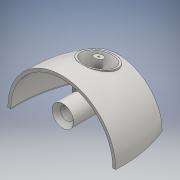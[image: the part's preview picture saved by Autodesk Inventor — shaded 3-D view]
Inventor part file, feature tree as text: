
AUTODESK INVENTOR PART (.ipt)
format: ipt  version: 2016 (Build 200138000, 138)  size: 376,320 bytes
history: native  units: mm
features: sketch x16, extrude x8, plane x6, other x4, loft x3, hole x2, shell x1, chamfer x1
ambient origin geometry x8: Origin, YZ Plane, XZ Plane, XY Plane, X Axis, Y Axis, Z Axis, Center Point
bodies: Solid1 (feature_tree)
feature tree (41):
  sketch  "Sketch1"  dims[d0=32.5mm d1=17.0mm]
  plane  "Work Plane1"
  sketch  "Sketch2"  dims[d2=26.5mm d3=4.0mm d4=32.5mm]
  plane  "Work Plane2"
  loft  "Loft1"
  extrude  "Extrusion1"  Depth=4.0mm
  plane  "Work Plane3"
  sketch  "Sketch5"  dims[d14=10.0mm d15=11.0mm]
  shell  "Shell1"  Thickness=32.5mm
  extrude  "Extrusion2"  TaperAngle=0.0deg  [1 undecoded]
  hole  "Hole1"  [1 undecoded]
  chamfer  "Chamfer1"  Distance=10.0mm
  extrude  "Extrusion3"  Depth=10.0mm
  plane  "Work Plane4"
  extrude  "Extrusion4"  Depth=0.9mm
  plane  "Work Plane5"
  sketch  "Sketch10"  dims[d31=5.0mm d32=0.0mm d33=5.6mm]
  other  "Work Point1"
  extrude  "Extrusion5"  Depth=15.8mm TaperAngle=0.0deg
  extrude  "Extrusion6"  Depth=1.3mm TaperAngle=45.0deg
  loft  "Loft2"
  sketch  "Sketch13"  dims[d39=3.5mm d40=0.0mm d41=3.5mm d42=0.0mm]
  plane  "Work Plane6"
  loft  "Loft3"
  extrude  "Extrusion7"  Depth=10.0mm
  extrude  "Extrusion8"  Depth=3.5mm TaperAngle=0.0deg
  hole  "Hole2"  [1 undecoded]
  sketch  "Sketch3"  dims[d5=0.0mm d6=90.0deg d7=0.0mm d8=90.0deg]
  sketch  "Sketch4"  dims[d9=0.0mm d10=90.0deg d11=16.5mm d12=10.0mm d13=0.0mm]
  sketch  "Sketch6"  dims[d16=0.9mm d17=6.5mm]
  sketch  "Sketch7"  dims[d18=5.75mm d19=15.8mm d20=0.0mm]
  sketch  "Sketch8"  dims[d21=3.9mm d22=6.0mm d23=4.0mm d24=2.0mm d25=90.0deg d26=5.0mm d27=20.594885mm d28=1.3mm d29=2.0mm d30=45.0deg]
  other  "Work Axis1"
  sketch  "Sketch11"  dims[d34=10.0mm d35=1.5mm d36=0.0mm]
  sketch  "Sketch12"  dims[d37=3.75mm d38=10.0mm]
  other  "Edges1"
  other  "Edges2"
  sketch  "Sketch14"  dims[d43=0.0mm d44=90.0deg d45=0.0mm d46=90.0deg]
  sketch  "Sketch15"  dims[d47=9.0mm]
  sketch  "Sketch16"  dims[d48=-5.0mm]
  sketch  "Sketch17"  dims[d49=4.0mm d51=0.0mm d52=90.0deg d53=0.0mm d54=90.0deg d55=2.6mm d56=5.7mm d57=0.0mm d58=0.6mm d59=5.7mm d60=0.0mm d61=8.0mm d62=8.0mm d63=1.7mm d64=6.0mm d65=4.0mm d66=2.0mm d67=90.0deg d68=8.0mm d69=20.594885mm]
note: 3 required parameter values undecoded (feature->parameter linkage not recoverable at this tier; creation-order binding heuristic only, values carry confidence <= 0.55)
